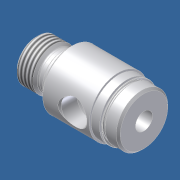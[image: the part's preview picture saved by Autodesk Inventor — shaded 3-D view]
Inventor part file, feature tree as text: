
AUTODESK INVENTOR PART (.ipt)
format: ipt  version: 2012 (Build 160160000, 160)  size: 240,640 bytes
history: native  units: in
note: dims shown in document units (in); Inventor stores cm internally (conversion verified against a paired STEP export)
features: other x106, revolve x6, sketch x6, thread x1
ambient origin geometry x8: Origin, YZ Plane, XZ Plane, XY Plane, X Axis, Y Axis, Z Axis, Center Point
bodies: Solid1 (feature_tree)
feature tree (119):
  other  "04R000_rod_guide"
  revolve  "Revolution1"  [1 undecoded]
  thread  "Thread1"  [1 undecoded]
  revolve  "Revolution2"  Angle=360.0deg
  revolve  "Revolution3"  Angle=360.0deg
  revolve  "Revolution4"  [1 undecoded]
  revolve  "Revolution5"  [1 undecoded]
  revolve  "Revolution6"  [1 undecoded]
  other  "s1_XY"
  other  "s1_YZ"
  other  "s1_ZX"
  other  "s1_X"
  other  "s1_Y"
  other  "s1_Z"
  other  "s1_Center"
  other  "s2_XY"
  other  "s2_YZ"
  other  "s2_ZX"
  other  "s2_X"
  other  "s2_Y"
  other  "s2_Z"
  other  "s2_Center"
  other  "dp1_XY"
  other  "dp1_YZ"
  other  "dp1_ZX"
  other  "dp1_X"
  other  "dp1_Y"
  other  "dp1_Z"
  other  "dp1_Center"
  other  "dp2_XY"
  other  "dp2_YZ"
  other  "dp2_ZX"
  other  "dp2_X"
  other  "dp2_Y"
  other  "dp2_Z"
  other  "dp2_Center"
  other  "rod_guide_XY"
  other  "rod_guide_YZ"
  other  "rod_guide_ZX"
  other  "rod_guide_X"
  other  "rod_guide_Y"
  other  "rod_guide_Z"
  other  "rod_guide_Center"
  other  "to_tube_XY"
  other  "to_tube_YZ"
  other  "to_tube_ZX"
  other  "to_tube_X"
  other  "to_tube_Y"
  other  "to_tube_Z"
  other  "to_tube_Center"
  other  "to_foot_bracket_XY"
  other  "to_foot_bracket_YZ"
  other  "to_foot_bracket_ZX"
  other  "to_foot_bracket_X"
  other  "to_foot_bracket_Y"
  other  "to_foot_bracket_Z"
  other  "to_foot_bracket_Center"
  other  "to_nut_XY"
  other  "to_nut_YZ"
  other  "to_nut_ZX"
  other  "to_nut_X"
  other  "to_nut_Y"
  other  "to_nut_Z"
  other  "to_nut_Center"
  other  "to_trunnion_brackets_XY"
  other  "to_trunnion_brackets_YZ"
  other  "to_trunnion_brackets_ZX"
  other  "to_trunnion_brackets_X"
  other  "to_trunnion_brackets_Y"
  other  "to_trunnion_brackets_Z"
  other  "to_trunnion_brackets_Center"
  other  "to_trunnion_brackets1_XY"
  other  "to_trunnion_brackets1_YZ"
  other  "to_trunnion_brackets1_ZX"
  other  "to_trunnion_brackets1_X"
  other  "to_trunnion_brackets1_Y"
  other  "to_trunnion_brackets1_Z"
  other  "to_trunnion_brackets1_Center"
  other  "to_trunnion_brackets2_XY"
  other  "to_trunnion_brackets2_YZ"
  other  "to_trunnion_brackets2_ZX"
  other  "to_trunnion_brackets2_X"
  other  "to_trunnion_brackets2_Y"
  other  "to_trunnion_brackets2_Z"
  other  "to_trunnion_brackets2_Center"
  other  "t111_XY"
  other  "t111_YZ"
  other  "t111_ZX"
  other  "t111_X"
  other  "t111_Y"
  other  "t111_Z"
  other  "t111_Center"
  other  "t1_XY"
  other  "t1_YZ"
  other  "t1_ZX"
  other  "t1_X"
  other  "t1_Y"
  other  "t1_Z"
  other  "t1_Center"
  other  "port_XY"
  other  "port_YZ"
  other  "port_ZX"
  other  "port_X"
  other  "port_Y"
  other  "port_Z"
  other  "port_Center"
  other  "to_screw_XY"
  other  "to_screw_YZ"
  other  "to_screw_ZX"
  other  "to_screw_X"
  other  "to_screw_Y"
  other  "to_screw_Z"
  other  "to_screw_Center"
  sketch  "Sketch_2"  dims[d0=360.0deg d1=0.2961in d2=0.0in d3=360.0deg]
  sketch  "Sketch_3"  dims[d4=360.0deg d5=360.0deg]
  sketch  "Sketch_5"  dims[d6=360.0deg d7=360.0deg]
  sketch  "Sketch_10"
  sketch  "Sketch_40"
  sketch  "Sketch_47"
note: 5 required parameter values undecoded (feature->parameter linkage not recoverable at this tier; creation-order binding heuristic only, values carry confidence <= 0.55)